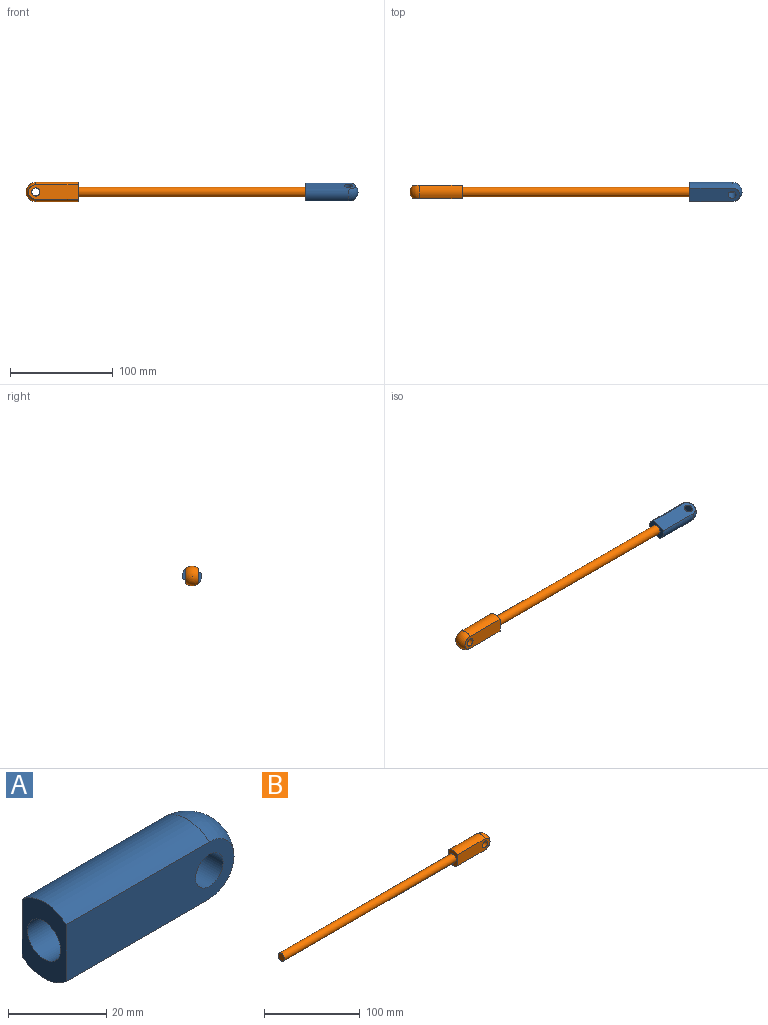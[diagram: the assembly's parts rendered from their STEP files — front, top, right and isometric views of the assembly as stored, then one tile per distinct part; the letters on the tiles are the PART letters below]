
ASSEMBLY  parts=2 mates=1
PART A: 9 faces, bbox 50.8x19.1x19.1 mm
  f0: sphere r=9.53mm, area 380mm2, adj f1,f2,f4,f5
  f1: cylinder r=9.53mm len=41.28mm, axis (-1,0,0), area 573.8mm2, adj f0,f3,f4,f5
  f2: cylinder r=9.53mm len=41.28mm, axis (-1,0,0), area 573.8mm2, adj f0,f3,f4,f5
  f3: plane 19.05x12.7mm, normal (-1,0,0), area 151.3mm2, adj f1,f2,f4,f5,f7
  f4: plane 48.37x14.2mm, normal (0,1,0), area 615.8mm2, adj f0,f1,f2,f3,f6
  f5: plane 48.37x14.2mm, normal (0,-1,0), area 615.8mm2, adj f0,f1,f2,f3,f6
  f6: cylinder r=3.97mm len=12.7mm, axis (0,-1,0), area 316.7mm2, adj f4,f5
  f7: cylinder r=4.76mm len=31.75mm, axis (-1,0,0), area 950.1mm2, adj f3,f8
  f8: plane 9.53x9.53mm, normal (-1,0,0), area 71.3mm2, adj f7
PART B: 9 faces, bbox 304.8x19.1x19.1 mm
  f0: sphere r=9.53mm, area 380mm2, adj f1,f2,f6,f7
  f1: cylinder r=9.53mm len=41.28mm, axis (-1,0,0), area 573.8mm2, adj f0,f3,f6,f7
  f2: cylinder r=9.53mm len=41.28mm, axis (-1,0,0), area 573.8mm2, adj f0,f3,f6,f7
  f3: plane 19.05x12.7mm, normal (-1,0,0), area 151.3mm2, adj f1,f2,f5,f6,f7
  f4: plane 9.53x9.53mm, normal (-1,0,0), area 71.3mm2, adj f5
  f5: cylinder r=4.76mm len=254mm, axis (-1,0,0), area 7600.6mm2, adj f3,f4
  f6: plane 48.37x14.2mm, normal (0,1,0), area 615.8mm2, adj f0,f1,f2,f3,f8
  f7: plane 48.37x14.2mm, normal (0,-1,0), area 615.8mm2, adj f0,f1,f2,f3,f8
  f8: cylinder r=3.97mm len=12.7mm, axis (0,-1,0), area 316.7mm2, adj f6,f7
PLACE A rot(axis=(-1,0,0),65.4deg) t=(263.53,0,0)mm
PLACE B rot(axis=(0,1,0),180deg) t=(295.28,0,0)mm
MATE revolute A.f7 <-> B.f1  axis (-1,0,0) through (295.28,0,0)mm
